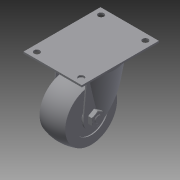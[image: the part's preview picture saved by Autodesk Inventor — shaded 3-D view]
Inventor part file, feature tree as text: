
AUTODESK INVENTOR PART (.ipt)
format: ipt  version: 2014 (Build 180170000, 170)  size: 275,968 bytes
history: native  units: in
note: dims shown in document units (in); Inventor stores cm internally (conversion verified against a paired STEP export)
features: imported_body x2, revolve x1, other x1, boolean_combine x1
ambient origin geometry x8: Origin, YZ Plane, XZ Plane, XY Plane, X Axis, Y Axis, Z Axis, Center Point
bodies: Body1 (feature_tree), Body2 (feature_tree)
feature tree (5):
  revolve  "Revolve1"  [1 undecoded]
  other  "2457T410_CART-SMART CASTER1"
  boolean_combine  "Combine4"
  imported_body  "Base1"
  imported_body  "Base2"
note: 1 required parameter value undecoded (feature->parameter linkage not recoverable at this tier; creation-order binding heuristic only, values carry confidence <= 0.55)
